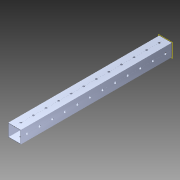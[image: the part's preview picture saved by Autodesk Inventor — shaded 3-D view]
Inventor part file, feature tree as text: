
AUTODESK INVENTOR PART (.ipt)
format: ipt  version: 2014 (Build 180170000, 170)  size: 1,181,184 bytes
history: native  units: in
note: dims shown in document units (in); Inventor stores cm internally (conversion verified against a paired STEP export)
features: pattern_circular x1, other x1, plane x1, extrude x1, imported_body x1, sketch x1
ambient origin geometry x8: Origin, YZ Plane, XZ Plane, XY Plane, X Axis, Y Axis, Z Axis, Center Point
bodies: Body1 (feature_tree)
feature tree (6):
  pattern_circular  "CirPattern2"
  other  "217-3426-STEP1"
  plane  "Work Plane1"
  extrude  "Extrusion1"  Depth=3937.0079in TaperAngle=0.0deg
  imported_body  "Base1"
  sketch  "Sketch1"  dims[d0=-12.0in d1=3937.0079in d2=0.0in]
